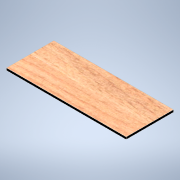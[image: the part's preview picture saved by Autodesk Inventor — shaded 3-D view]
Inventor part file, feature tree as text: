
AUTODESK INVENTOR PART (.ipt)
format: ipt  version: 2021 (Build 250183000, 183)  size: 121,344 bytes
history: native  units: mm
features: extrude x1, sketch x1
ambient origin geometry x8: Origin, YZ Plane, XZ Plane, XY Plane, X Axis, Y Axis, Z Axis, Center Point
bodies: Volumenkörper1 (feature_tree)
feature tree (2):
  extrude  "Extrusion1"  Depth=65.5mm
  sketch  "Skizze1"  dims[d0=165.5mm d1=65.5mm d2=3.0mm d3=0.0mm d4=21.0mm d5=18.0mm d6=50.0mm]
